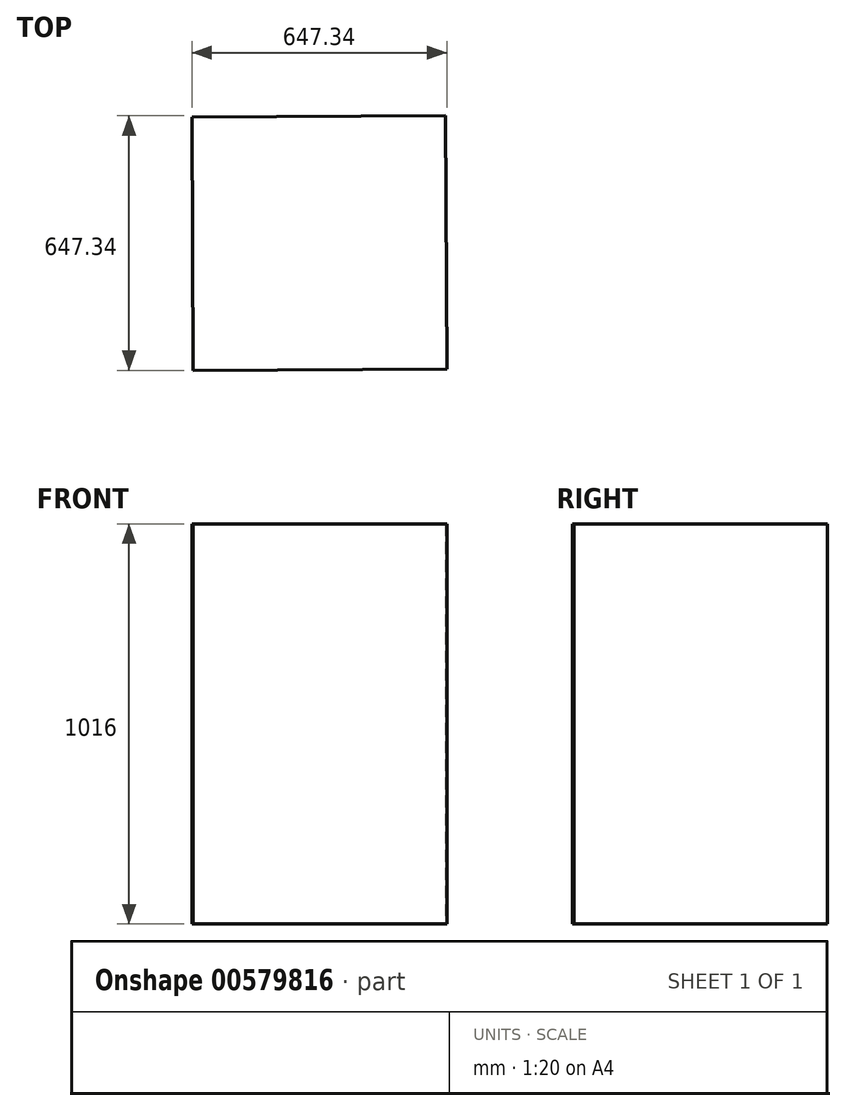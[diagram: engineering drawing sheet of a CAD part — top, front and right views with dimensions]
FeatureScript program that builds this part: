
annotation { "Feature Type Name" : "Feature", "Feature Type Description" : "" }
export const myFeature = defineFeature(function(context is Context, id is Id, definition is map)
    precondition{}
    {
        {
            var Q0;
            Q0=qCreatedBy(makeId("Top.planeOp"),FACE);
            var sketch = newSketch(context, id + "F0", { "sketchPlane" : qUnion([Q0])});
            skCircle(sketch, "E0.cCircle", {"center": v(0, 0) * mm, "radius": 322.07 * mm, "construction": true});
            skLineSegment(sketch, "E0.0", {"start": v(320.46, 323.67) * mm, "end": v(323.67, -320.46) * mm});
            skLineSegment(sketch, "E0.1", {"start": v(323.67, -320.46) * mm, "end": v(-320.46, -323.67) * mm});
            skLineSegment(sketch, "E0.2", {"start": v(-320.46, -323.67) * mm, "end": v(-323.67, 320.46) * mm});
            skLineSegment(sketch, "E0.3", {"start": v(-323.67, 320.46) * mm, "end": v(320.46, 323.67) * mm});
            skPoint(sketch, "E0.0.midPoint", {"position": v(322.07, 1.6) * mm});
            skSolve(sketch);
        }
        {
            var Q0;
            Q0=makeQuery(id+"F0.imprint","IMPRINT",FACE,{"disambiguationData":[TD([[makeQuery(id+"F0.imprint","IMPRINT",EDGE,{"derivedFrom":sQuery(id+"F0.wireOp",EDGE,"E0.0")}),-1.0]])]});
            extrude(context, id + "F1", {"entities" : qUnion([Q0]), "depth" : 1016 * mm, "offsetDistance" : 25.4 * mm});
        }
    });
